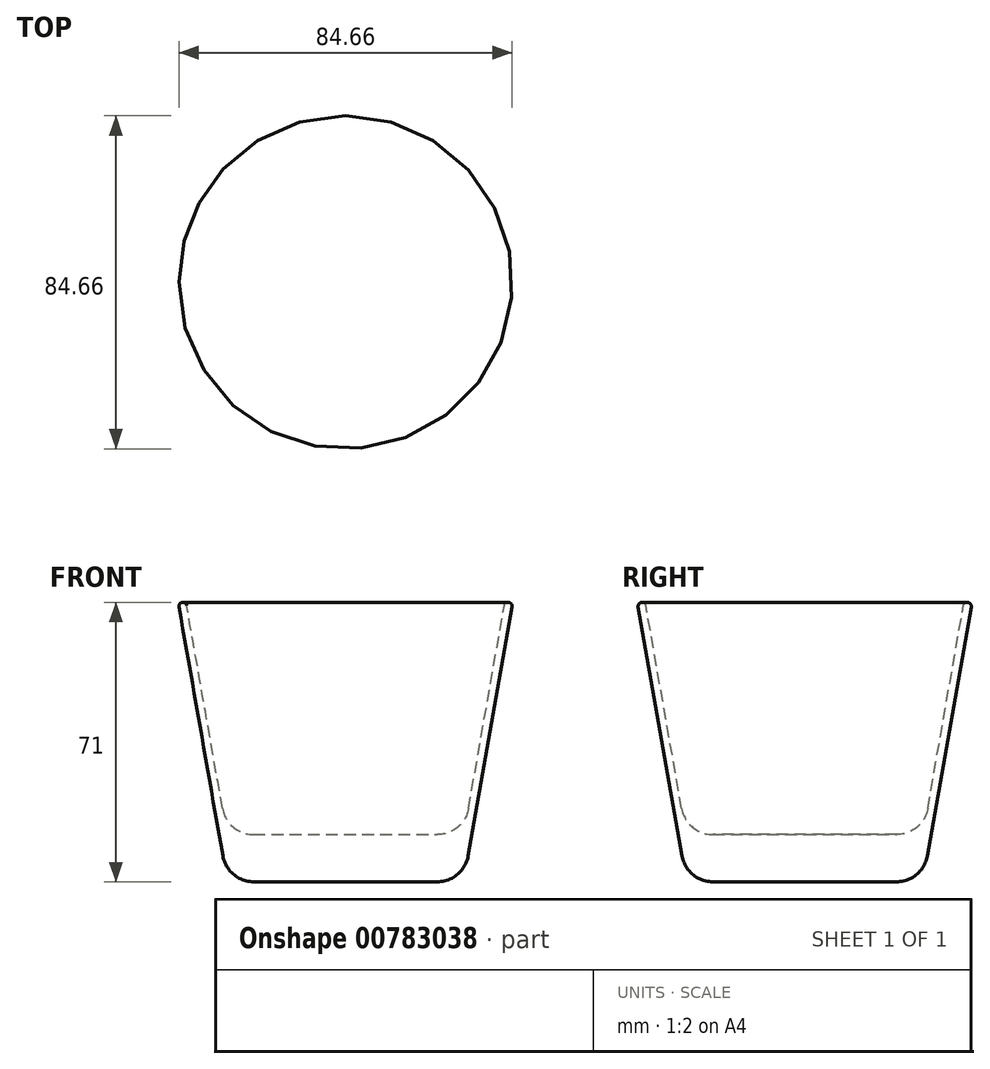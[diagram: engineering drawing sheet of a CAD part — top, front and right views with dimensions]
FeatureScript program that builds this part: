
annotation { "Feature Type Name" : "Feature", "Feature Type Description" : "" }
export const myFeature = defineFeature(function(context is Context, id is Id, definition is map)
    precondition{}
    {
        {
            var Q0;
            Q0=qCreatedBy(makeId("Front.planeOp"),FACE);
            var sketch = newSketch(context, id + "F0", { "sketchPlane" : qUnion([Q0])});
            skLineSegment(sketch, "E0", {"start": v(0, 0) * mm, "end": v(23.29, 0) * mm});
            skLineSegment(sketch, "E1", {"start": v(31.17, 6.61) * mm, "end": v(42.31, 69.83) * mm});
            skPoint(sketch, "E2.visualSharp", {"position": v(30, 0) * mm});
            skArc(sketch, "E2.filletArc", {"start": v(23.29, 0) * mm, "mid": v(28.43, 1.87) * mm, "end": v(31.17, 6.61) * mm});
            skLineSegment(sketch, "E3.0", {"start": v(31.25, 18.61) * mm, "end": v(40.34, 70.17) * mm});
            skLineSegment(sketch, "E4.0", {"start": v(0, 12) * mm, "end": v(23.37, 12) * mm});
            skArc(sketch, "E5.filletArc", {"start": v(23.37, 12) * mm, "mid": v(28.51, 13.87) * mm, "end": v(31.25, 18.61) * mm});
            skArc(sketch, "E6", {"start": v(42.31, 69.83) * mm, "mid": v(41.5, 70.98) * mm, "end": v(40.34, 70.17) * mm});
            skPoint(sketch, "E6.first.point", {"position": v(40.34, 70.17) * mm});
            skPoint(sketch, "E6.second.point", {"position": v(40.5, 70.55) * mm});
            skPoint(sketch, "E6.third.point", {"position": v(42.31, 69.83) * mm});
            skPoint(sketch, "E7.orphan", {"position": v(42.2, 69.18) * mm});
            skLineSegment(sketch, "E8", {"start": v(0, 0) * mm, "end": v(0, 12) * mm});
            skSolve(sketch);
        }
        {
            var Q0;
            Q0=makeQuery(id+"F0.imprint","IMPRINT",FACE,{"disambiguationData":[TD([[makeQuery(id+"F0.imprint","IMPRINT",EDGE,{"derivedFrom":sQuery(id+"F0.wireOp",EDGE,"E0")}),1.0]])]});
            var Q1;
            Q1=sQuery(id+"F0.wireOp",EDGE,"E8");
            revolve(context, id + "F1", {"surfaceOperationType" : NewSurfaceOperationType.NEW, "entities" : qUnion([Q0]), "axis" : qUnion([Q1]), "revolveType" : RevolveType.FULL});
        }
    });
